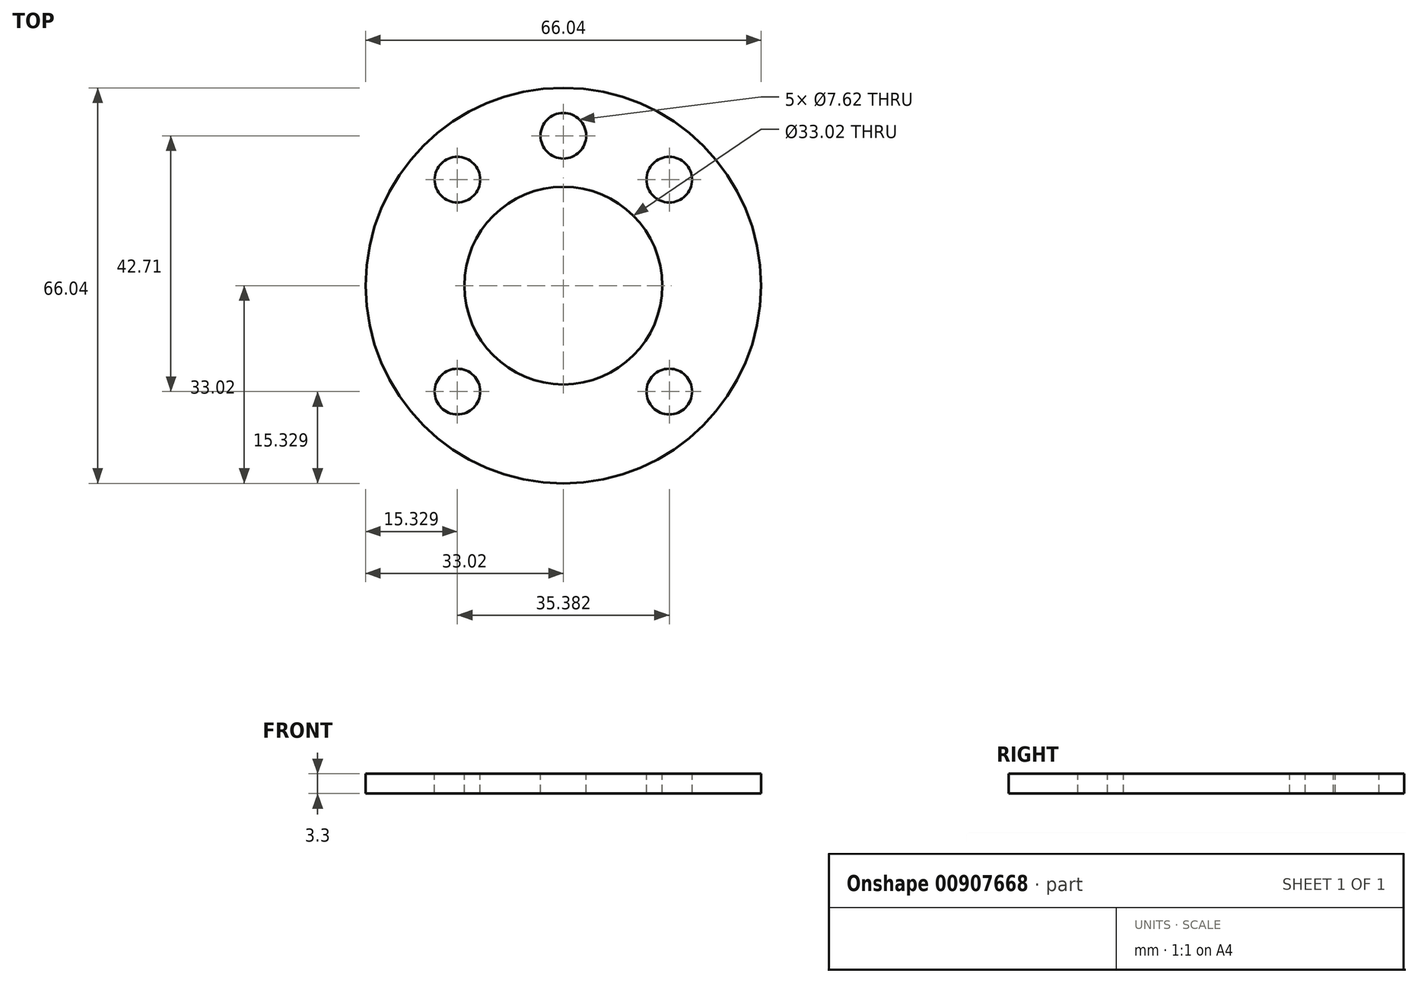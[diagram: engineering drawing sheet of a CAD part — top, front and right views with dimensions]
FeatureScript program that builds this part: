
annotation { "Feature Type Name" : "Feature", "Feature Type Description" : "" }
export const myFeature = defineFeature(function(context is Context, id is Id, definition is map)
    precondition{}
    {
        {
            var Q0;
            Q0=qCreatedBy(makeId("Top.planeOp"),FACE);
            var sketch = newSketch(context, id + "F0", { "sketchPlane" : qUnion([Q0])});
            skCircle(sketch, "E0", {"center": v(0, 0) * mm, "radius": 33.02 * mm});
            skSolve(sketch);
        }
        {
            var Q0;
            Q0 = qSketchRegion(id + "F0", true);
            extrude(context, id + "F1", {"entities" : qUnion([Q0]), "depth" : 3.3 * mm, "offsetDistance" : 25.4 * mm});
        }
        {
            var Q0;
            Q0=makeQuery(id+"F1.opExtrude","CAP_FACE",FACE,{"disambiguationData":[OSD([sQuery(id+"F0.wireOp",EDGE,"E0")])],"isStart":false});
            var sketch = newSketch(context, id + "F2", { "sketchPlane" : qUnion([Q0])});
            skCircle(sketch, "E1", {"center": v(0, 0) * mm, "radius": 16.51 * mm});
            skSolve(sketch);
        }
        {
            var Q0;
            Q0 = qSketchRegion(id + "F2", true);
            extrude(context, id + "F3", {"entities" : qUnion([Q0]), "operationType" : NewBodyOperationType.REMOVE, "endBound" : BoundingType.THROUGH_ALL, "oppositeDirection" : true, "depth" : 25.4 * mm, "offsetDistance" : 25.4 * mm});
        }
        {
            var Q0;
            Q0=makeQuery(id+"F1.opExtrude","CAP_FACE",FACE,{"disambiguationData":[OSD([sQuery(id+"F0.wireOp",EDGE,"E0")])],"isStart":false});
            var sketch = newSketch(context, id + "F4", { "sketchPlane" : qUnion([Q0])});
            skLineSegment(sketch, "E2", {"start": v(-33.02, 0) * mm, "end": v(33.02, 0) * mm});
            skCircle(sketch, "E3", {"center": v(0, 0) * mm, "radius": 25.02 * mm});
            skPoint(sketch, "E4", {"position": v(0, 25.02) * mm});
            skLineSegment(sketch, "E5", {"start": v(-17.7, -17.7) * mm, "end": v(17.7, 17.7) * mm});
            skPoint(sketch, "E6", {"position": v(17.7, 17.7) * mm});
            skPoint(sketch, "E7", {"position": v(-17.7, 17.7) * mm});
            skPoint(sketch, "E8", {"position": v(-17.7, -17.7) * mm});
            skPoint(sketch, "E9", {"position": v(17.7, -17.7) * mm});
            skSolve(sketch);
        }
        {
            var Q0;
            Q0=sQuery(id+"F4.wireOp",VERTEX,"E9");
            var Q1;
            Q1=sQuery(id+"F4.wireOp",VERTEX,"E8");
            var Q2;
            Q2=sQuery(id+"F4.wireOp",VERTEX,"E6");
            var Q3;
            Q3=sQuery(id+"F4.wireOp",VERTEX,"E4");
            var Q4;
            Q4=sQuery(id+"F4.wireOp",VERTEX,"E7");
            var Q5;
            Q5=makeQuery(id+"F1.opExtrude","SWEPT_BODY",BODY,{"disambiguationData":[OSD([sQuery(id+"F0.wireOp",EDGE,"E0")])]});
            hole(context, id + "F5", {"style" : HoleStyle.SIMPLE, "endStyle" : HoleEndStyle.THROUGH, "holeDiameter" : 7.62 * mm, "majorDiameter" : 6.35 * mm, "isTappedThrough" : true, "tappedDepth" : 12.7 * mm, "tapClearance" : 3, "startFromSketch" : true, "locations" : qUnion([Q0, Q1, Q2, Q3, Q4]), "scope" : qUnion([Q5])});
        }
    });
